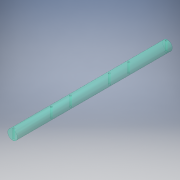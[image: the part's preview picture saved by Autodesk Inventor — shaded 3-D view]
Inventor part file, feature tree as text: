
AUTODESK INVENTOR PART (.ipt)
format: ipt  version: 2016 (Build 200138000, 138)  size: 129,024 bytes
history: native  units: in
note: dims shown in document units (in); Inventor stores cm internally (conversion verified against a paired STEP export)
features: extrude x3, sketch x3
ambient origin geometry x8: Origin, YZ Plane, XZ Plane, XY Plane, X Axis, Y Axis, Z Axis, Center Point
bodies: Solid1 (feature_tree)
feature tree (6):
  extrude  "Extrusion1"  Depth=8.0in TaperAngle=0.0deg
  extrude  "Extrusion4"  Depth=0.06in
  extrude  "Extrusion10"  Depth=2.0in TaperAngle=0.0deg
  sketch  "Sketch1"  dims[d0=0.5in d1=8.0in d2=0.0in]
  sketch  "Sketch4"  dims[d13=0.06in d15=0.06in]
  sketch  "Sketch8"  dims[d16=0.1in d17=0.6in d18=0.0in d19=0.1in d50=2.0in d51=0.1in d58=1.0in d59=0.1in d60=2.0in d61=0.1in d62=1.0in d63=0.1in d64=1.0in d65=0.0in]
